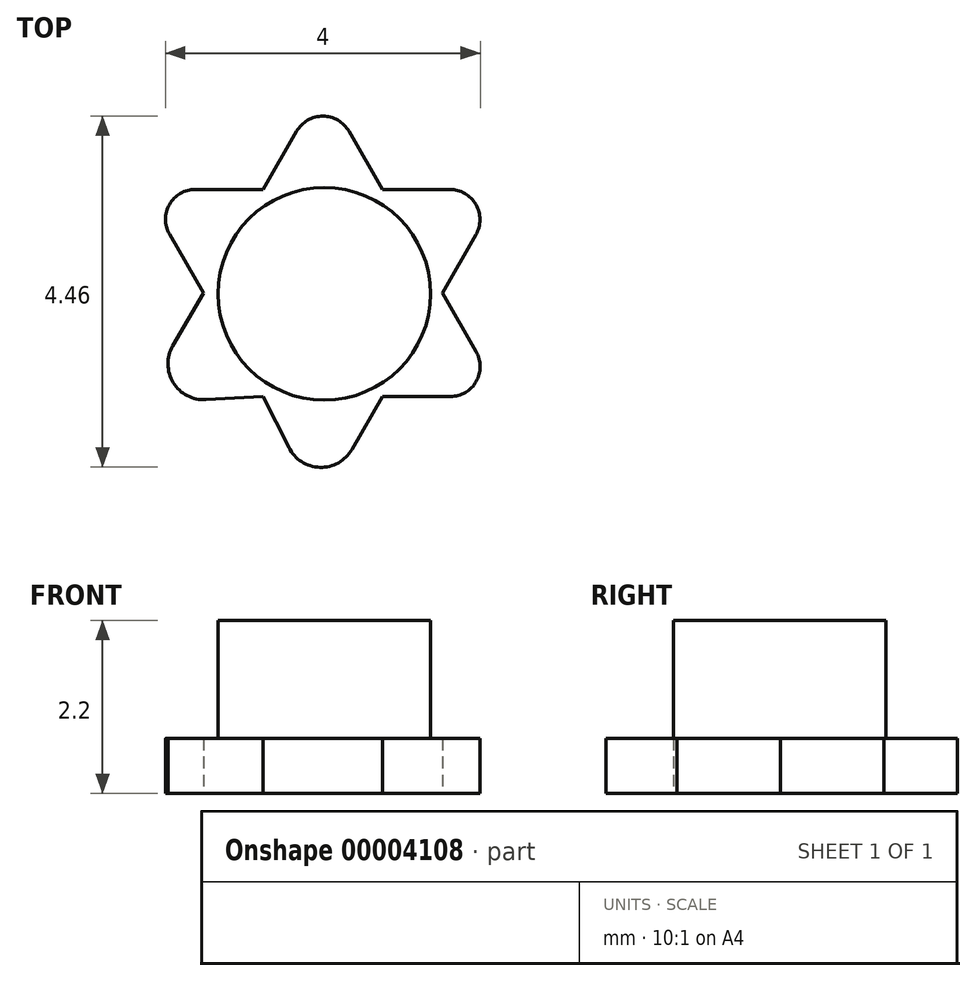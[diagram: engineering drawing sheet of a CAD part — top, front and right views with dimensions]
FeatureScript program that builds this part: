
annotation { "Feature Type Name" : "Feature", "Feature Type Description" : "" }
export const myFeature = defineFeature(function(context is Context, id is Id, definition is map)
    precondition{}
    {
        {
            var Q0;
            Q0=qCreatedBy(makeId("Top.planeOp"),FACE);
            var sketch = newSketch(context, id + "F0", { "sketchPlane" : qUnion([Q0])});
            skPoint(sketch, "E0", {"position": v(-5.67, 3.57) * mm});
            skPoint(sketch, "E1", {"position": v(-4.15, 3.57) * mm});
            skPoint(sketch, "E2", {"position": v(-6.43, 2.26) * mm});
            skPoint(sketch, "E3", {"position": v(-5.67, 0.95) * mm});
            skPoint(sketch, "E4", {"position": v(-6.86, 3) * mm});
            skLineSegment(sketch, "E5", {"start": v(-5.67, 0.95) * mm, "end": v(-4.15, 3.57) * mm, "construction": true});
            skLineSegment(sketch, "E6", {"start": v(-6.86, 3) * mm, "end": v(-6.43, 2.26) * mm});
            skLineSegment(sketch, "E7", {"start": v(-6.53, 3.57) * mm, "end": v(-5.67, 3.57) * mm});
            skArc(sketch, "E8", {"start": v(-6.53, 3.57) * mm, "mid": v(-6.86, 3.39) * mm, "end": v(-6.86, 3) * mm});
            skPoint(sketch, "E9", {"position": v(-5.24, 4.31) * mm});
            skPoint(sketch, "E10", {"position": v(-4.58, 4.31) * mm});
            skPoint(sketch, "E11", {"position": v(-6.82, 1.59) * mm});
            skPoint(sketch, "E12", {"position": v(-6.4, 0.95) * mm});
            skLineSegment(sketch, "E13", {"start": v(-6.43, 2.26) * mm, "end": v(-6.82, 1.59) * mm});
            skLineSegment(sketch, "E14", {"start": v(-6.4, 0.9) * mm, "end": v(-5.67, 0.95) * mm});
            skLineSegment(sketch, "E15", {"start": v(-5.67, 3.57) * mm, "end": v(-5.24, 4.31) * mm});
            skLineSegment(sketch, "E16", {"start": v(-4.58, 4.31) * mm, "end": v(-4.15, 3.57) * mm});
            skArc(sketch, "E17", {"start": v(-4.58, 4.31) * mm, "mid": v(-4.91, 4.5) * mm, "end": v(-5.24, 4.31) * mm});
            skArc(sketch, "E18", {"start": v(-6.82, 1.59) * mm, "mid": v(-6.81, 1.12) * mm, "end": v(-6.4, 0.9) * mm});
            skLineSegment(sketch, "E19.0.MirrorCS", {"start": v(-2.96, 1.51) * mm, "end": v(-3.4, 2.26) * mm});
            skLineSegment(sketch, "E19.1.MirrorCS", {"start": v(-3.3, 0.95) * mm, "end": v(-4.15, 0.95) * mm});
            skPoint(sketch, "E19.2.MirrorP", {"position": v(-3.4, 2.26) * mm});
            skLineSegment(sketch, "E19.3.MirrorCS", {"start": v(-3.4, 2.26) * mm, "end": v(-2.97, 3) * mm});
            skLineSegment(sketch, "E19.4.MirrorCS", {"start": v(-5.34, 0.3) * mm, "end": v(-5.67, 0.95) * mm});
            skPoint(sketch, "E19.5.MirrorP", {"position": v(-4.15, 0.95) * mm});
            skArc(sketch, "E19.6.MirrorCS", {"start": v(-3.3, 3.57) * mm, "mid": v(-2.97, 3.38) * mm, "end": v(-2.97, 3) * mm});
            skPoint(sketch, "E19.7.MirrorP", {"position": v(-4.54, 0.27) * mm});
            skPoint(sketch, "E19.10.MirrorP", {"position": v(-2.97, 3) * mm});
            skPoint(sketch, "E19.11.MirrorP", {"position": v(-5.3, 0.32) * mm});
            skPoint(sketch, "E19.12.MirrorP", {"position": v(-3.3, 3.57) * mm});
            skPoint(sketch, "E19.13.MirrorP", {"position": v(-3.3, 0.95) * mm});
            skArc(sketch, "E19.14.MirrorCS", {"start": v(-4.54, 0.27) * mm, "mid": v(-4.95, 0.05) * mm, "end": v(-5.34, 0.3) * mm});
            skArc(sketch, "E19.15.MirrorCS", {"start": v(-2.96, 1.51) * mm, "mid": v(-2.96, 1.14) * mm, "end": v(-3.3, 0.95) * mm});
            skLineSegment(sketch, "E19.16.MirrorCS", {"start": v(-4.15, 0.95) * mm, "end": v(-4.54, 0.27) * mm});
            skLineSegment(sketch, "E19.17.MirrorCS", {"start": v(-3.3, 3.57) * mm, "end": v(-4.15, 3.57) * mm});
            skLineSegment(sketch, "E20", {"start": v(-6.86, 3.39) * mm, "end": v(-2.96, 1.14) * mm, "construction": true});
            skSolve(sketch);
        }
        {
            var Q0;
            Q0=makeQuery(id+"F0.imprint","IMPRINT",FACE,{"disambiguationData":[TD([[makeQuery(id+"F0.imprint","IMPRINT",EDGE,{"derivedFrom":sQuery(id+"F0.wireOp",EDGE,"E6")}),1.0]])]});
            extrude(context, id + "F1", {"entities" : qUnion([Q0]), "depth" : 0.7 * mm});
        }
        {
            var Q0;
            Q0=makeQuery(id+"F1.opExtrude","CAP_FACE",FACE,{"disambiguationData":[OSD([sQuery(id+"F0.wireOp",EDGE,"E6"),sQuery(id+"F0.wireOp",EDGE,"E7"),sQuery(id+"F0.wireOp",EDGE,"E8"),sQuery(id+"F0.wireOp",EDGE,"E13"),sQuery(id+"F0.wireOp",EDGE,"E14"),sQuery(id+"F0.wireOp",EDGE,"E15"),sQuery(id+"F0.wireOp",EDGE,"E16"),sQuery(id+"F0.wireOp",EDGE,"E17"),sQuery(id+"F0.wireOp",EDGE,"E18"),sQuery(id+"F0.wireOp",EDGE,"E19.0.MirrorCS"),sQuery(id+"F0.wireOp",EDGE,"E19.1.MirrorCS"),sQuery(id+"F0.wireOp",EDGE,"E19.3.MirrorCS"),sQuery(id+"F0.wireOp",EDGE,"E19.4.MirrorCS"),sQuery(id+"F0.wireOp",EDGE,"E19.6.MirrorCS"),sQuery(id+"F0.wireOp",EDGE,"E19.14.MirrorCS"),sQuery(id+"F0.wireOp",EDGE,"E19.15.MirrorCS"),sQuery(id+"F0.wireOp",EDGE,"E19.16.MirrorCS"),sQuery(id+"F0.wireOp",EDGE,"E19.17.MirrorCS")])],"isStart":false});
            var sketch = newSketch(context, id + "F2", { "sketchPlane" : qUnion([Q0])});
            skLineSegment(sketch, "E21", {"start": v(-6.86, 3.39) * mm, "end": v(-2.96, 1.14) * mm, "construction": true});
            skLineSegment(sketch, "E22", {"start": v(-2.97, 3.38) * mm, "end": v(-6.81, 1.12) * mm, "construction": true});
            skPoint(sketch, "E23", {"position": v(-4.9, 2.25) * mm});
            skCircle(sketch, "E24", {"center": v(-4.9, 2.25) * mm, "radius": 1.35 * mm});
            skSolve(sketch);
        }
        {
            var Q0;
            Q0=makeQuery(id+"F2.imprint","IMPRINT",FACE,{"disambiguationData":[TD([[makeQuery(id+"F2.imprint","IMPRINT",EDGE,{"derivedFrom":sQuery(id+"F2.wireOp",EDGE,"E24")}),1.0]])]});
            extrude(context, id + "F3", {"entities" : qUnion([Q0]), "operationType" : NewBodyOperationType.ADD, "depth" : 1.5 * mm});
        }
    });
